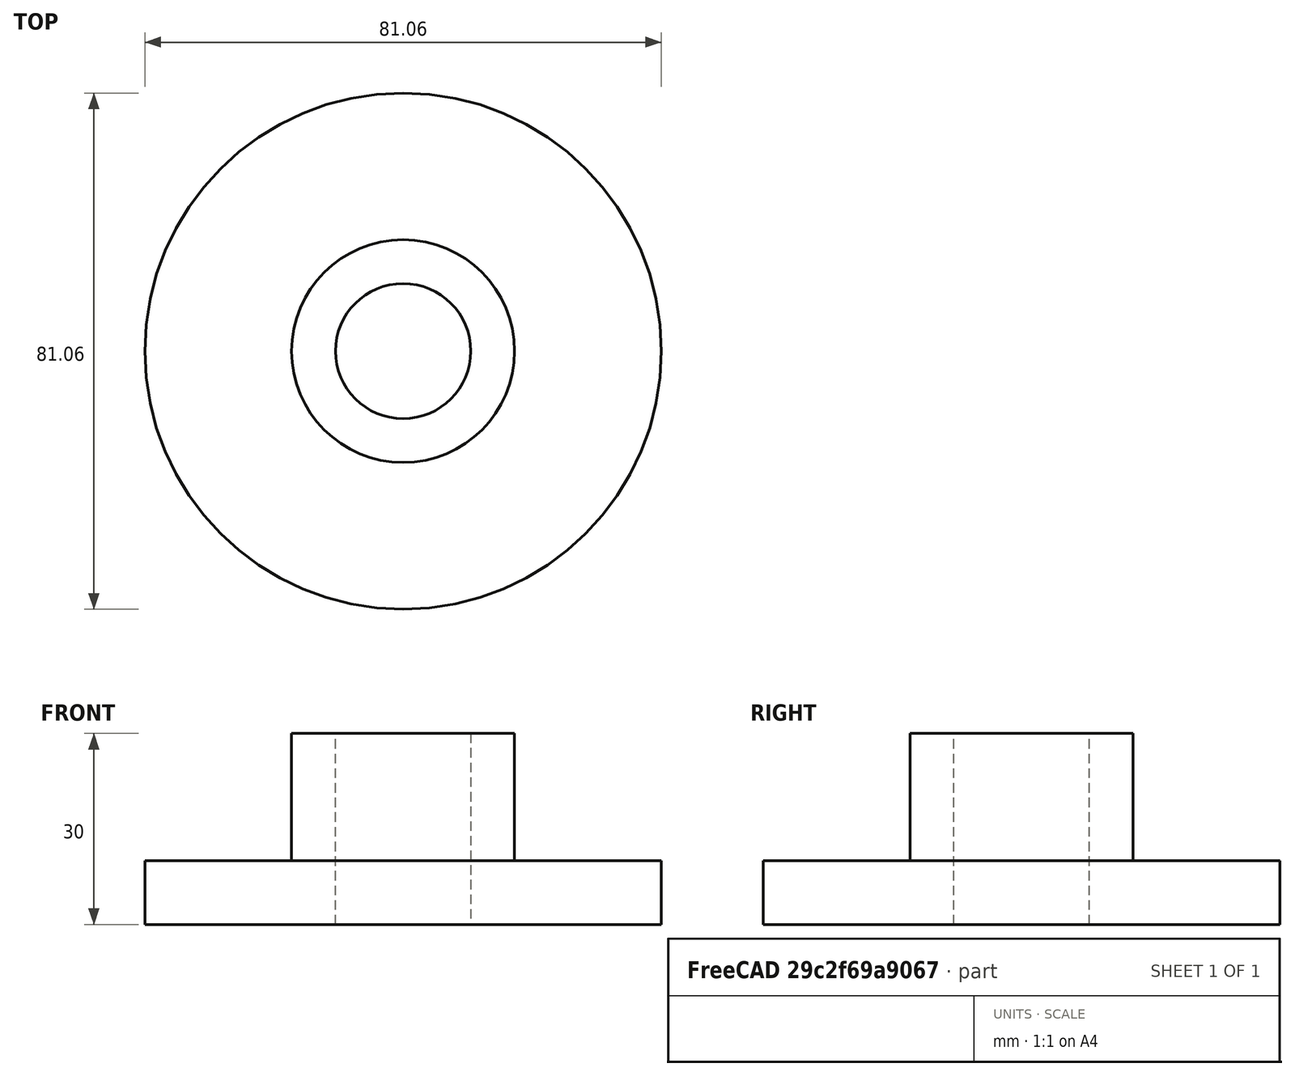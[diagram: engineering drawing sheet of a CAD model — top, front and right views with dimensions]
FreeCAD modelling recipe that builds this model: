
FCSTD DOCUMENT  (FreeCAD 0.15R4671 (Git))
Label: SGB_BearingLock
License: All rights reserved
LicenseURL: http://en.wikipedia.org/wiki/All_rights_reserved
objects: Sketcher::SketchObject×3, PartDesign::Pad×2, PartDesign::Pocket×1
note: 9 computed .brp shape members not serialized (recipe doc carries the construction recipe); baked Part::Feature solids carry a one-line shape summary decoded from their .brp

FEATURE [Sketcher::SketchObject] Sketch  label="BaseSketch"
  sketch-geometry (1):
    g0: Circle CenterX=0 CenterY=0 CenterZ=0 NormalX=0 NormalY=0 NormalZ=1 Radius=40.5271
  constraints (1):
    c: Coincident(g0,g-1)
FEATURE [PartDesign::Pad] Pad  label="Base"
  Length = 10
  Length2 = 100
  Sketch = -> Sketch
  Type = 0
FEATURE [Sketcher::SketchObject] Sketch001  label="InsertSketch"
  Placement = pos=(0,0,10) rot=(0,0,1;0rad)
  Support = -> Pad [Face3]
  sketch-geometry (1):
    g0: Circle CenterX=0 CenterY=0 CenterZ=0 NormalX=0 NormalY=0 NormalZ=1 Radius=17.4966
  constraints (1):
    c: Coincident(g0,g-1)
FEATURE [PartDesign::Pad] Pad001  label="Insert"
  Length = 20
  Length2 = 100
  Sketch = -> Sketch001
  Type = 0
FEATURE [Sketcher::SketchObject] Sketch002  label="ThroughHoleSketch"
  Placement = pos=(0,0,30) rot=(0,0,1;0rad)
  Support = -> Pad001 [Face5]
  sketch-geometry (1):
    g0: Circle CenterX=0 CenterY=0 CenterZ=0 NormalX=0 NormalY=0 NormalZ=1 Radius=10.6119
  constraints (1):
    c: Coincident(g0,g-1)
FEATURE [PartDesign::Pocket] Pocket  label="ThroughHole"
  Length = 30
  Sketch = -> Sketch002
  Type = 0
